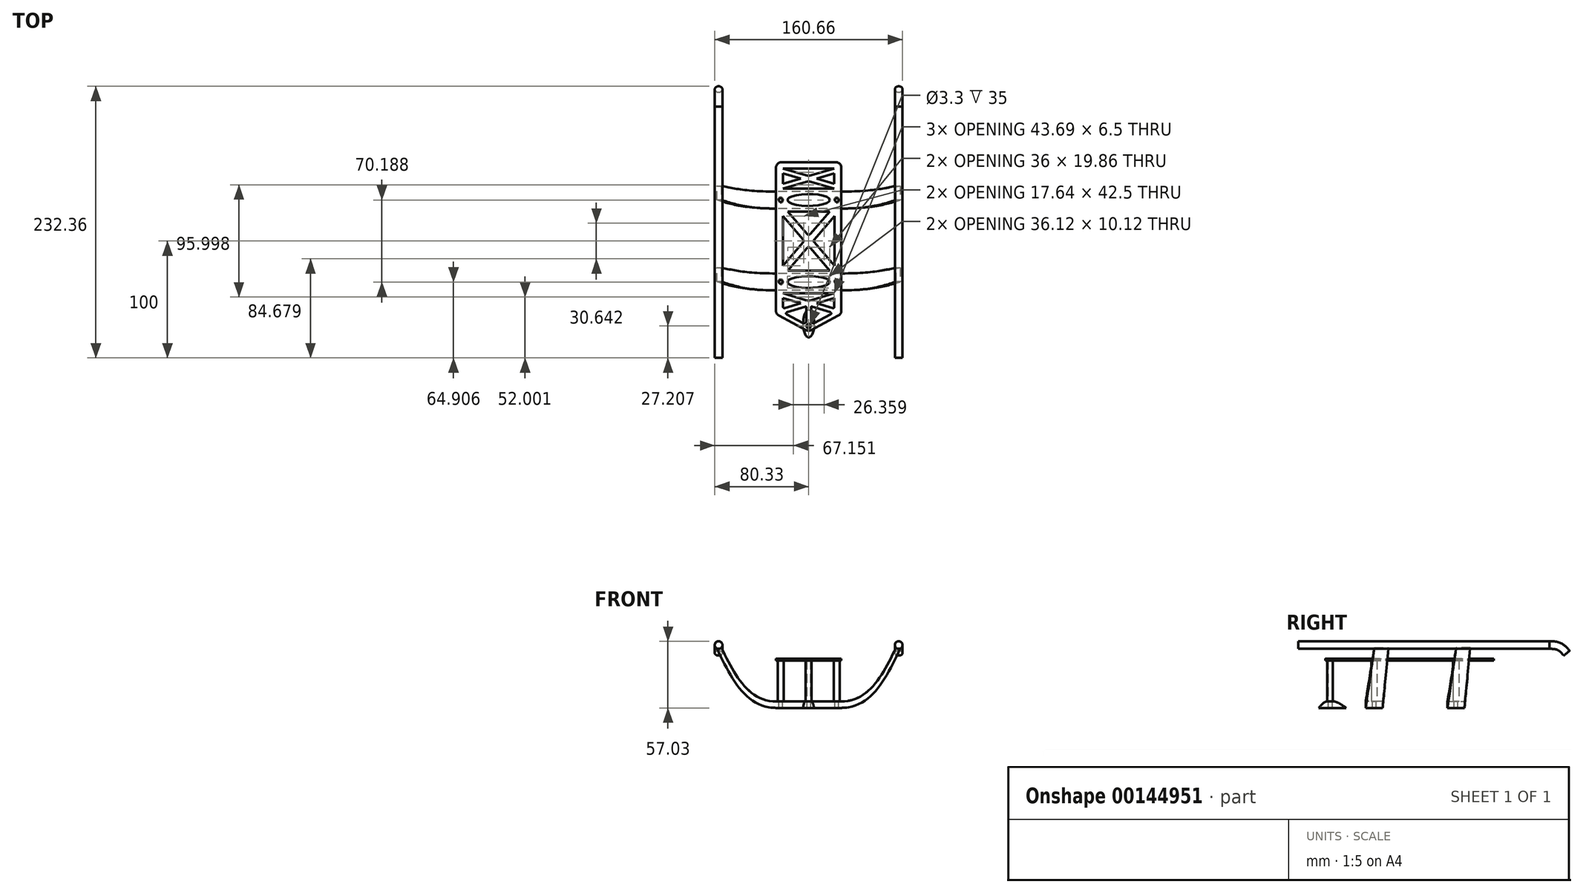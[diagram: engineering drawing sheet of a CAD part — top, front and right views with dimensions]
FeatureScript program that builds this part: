
annotation { "Feature Type Name" : "Feature", "Feature Type Description" : "" }
export const myFeature = defineFeature(function(context is Context, id is Id, definition is map)
    precondition{}
    {
        {
            var Q0;
            Q0=qCreatedBy(makeId("Top.planeOp"),FACE);
            var sketch = newSketch(context, id + "F0", { "sketchPlane" : qUnion([Q0])});
            skCircle(sketch, "E0", {"center": v(24, 35) * mm, "radius": 1.55 * mm});
            skCircle(sketch, "E1.MirrorC", {"center": v(-24, 35) * mm, "radius": 1.55 * mm});
            skCircle(sketch, "E2.MirrorC", {"center": v(-24, -35) * mm, "radius": 1.55 * mm});
            skCircle(sketch, "E3.MirrorC", {"center": v(24, -35) * mm, "radius": 1.55 * mm});
            skLineSegment(sketch, "E4.bottom", {"start": v(27.5, 27.75) * mm, "end": v(-27.5, 27.75) * mm});
            skLineSegment(sketch, "E4.top", {"start": v(27.5, 42.25) * mm, "end": v(-27.5, 42.25) * mm});
            skLineSegment(sketch, "E4.left", {"start": v(27.5, 27.75) * mm, "end": v(27.5, 42.25) * mm});
            skLineSegment(sketch, "E4.right", {"start": v(-27.5, 27.75) * mm, "end": v(-27.5, 42.25) * mm});
            skPoint(sketch, "E4.middle", {"position": v(0, 35) * mm});
            skPoint(sketch, "E5.MirrorP", {"position": v(0, -35) * mm});
            skLineSegment(sketch, "E6.MirrorCS", {"start": v(-27.5, -27.75) * mm, "end": v(-27.5, -42.25) * mm});
            skLineSegment(sketch, "E7.MirrorCS", {"start": v(27.5, -27.75) * mm, "end": v(27.5, -42.25) * mm});
            skLineSegment(sketch, "E8.MirrorCS", {"start": v(27.5, -27.75) * mm, "end": v(-27.5, -27.75) * mm});
            skLineSegment(sketch, "E9.MirrorCS", {"start": v(27.5, -42.25) * mm, "end": v(-27.5, -42.25) * mm});
            skSolve(sketch);
        }
        {
            var Q0;
            Q0=qSketchRegion(id+"F0",true);
            extrude(context, id + "F1", {"entities" : qUnion([Q0]), "oppositeDirection" : true, "depth" : 5.5 * mm});
        }
        {
            var Q0;
            Q0=makeQuery(id+"F1.opExtrude","CAP_FACE",FACE,{"disambiguationData":[OSD([sQuery(id+"F0.wireOp",EDGE,"E0"),sQuery(id+"F0.wireOp",EDGE,"E1.MirrorC"),sQuery(id+"F0.wireOp",EDGE,"E4.bottom"),sQuery(id+"F0.wireOp",EDGE,"E4.top"),sQuery(id+"F0.wireOp",EDGE,"E4.left"),sQuery(id+"F0.wireOp",EDGE,"E4.right")])],"isStart":true});
            cPlane(context, id + "F2", {"entities" : qUnion([Q0]), "cplaneType" : CPlaneType.OFFSET, "offset" : 47 * mm, "width" : 150 * mm, "height" : 150 * mm});
        }
        {
            var Q0;
            Q0=qCreatedBy(id+"F2.planeOp",FACE);
            var sketch = newSketch(context, id + "F3", { "sketchPlane" : qUnion([Q0])});
            skLineSegment(sketch, "E10.bottom", {"start": v(-79, 47.25) * mm, "end": v(-75, 47.25) * mm});
            skLineSegment(sketch, "E10.top", {"start": v(-79, 35.25) * mm, "end": v(-75, 35.25) * mm});
            skLineSegment(sketch, "E10.left", {"start": v(-79, 47.25) * mm, "end": v(-79, 35.25) * mm});
            skLineSegment(sketch, "E10.right", {"start": v(-75, 47.25) * mm, "end": v(-75, 35.25) * mm});
            skLineSegment(sketch, "E11.bottom", {"start": v(-79, -22.75) * mm, "end": v(-75, -22.75) * mm});
            skLineSegment(sketch, "E11.top", {"start": v(-79, -34.75) * mm, "end": v(-75, -34.75) * mm});
            skLineSegment(sketch, "E11.left", {"start": v(-79, -22.75) * mm, "end": v(-79, -34.75) * mm});
            skLineSegment(sketch, "E11.right", {"start": v(-75, -22.75) * mm, "end": v(-75, -34.75) * mm});
            skLineSegment(sketch, "E12.MirrorCS", {"start": v(79, 47.25) * mm, "end": v(75, 47.25) * mm});
            skLineSegment(sketch, "E13.MirrorCS", {"start": v(79, 35.25) * mm, "end": v(75, 35.25) * mm});
            skLineSegment(sketch, "E14.MirrorCS", {"start": v(79, 47.25) * mm, "end": v(79, 35.25) * mm});
            skLineSegment(sketch, "E15.MirrorCS", {"start": v(75, 47.25) * mm, "end": v(75, 35.25) * mm});
            skLineSegment(sketch, "E16.MirrorCS", {"start": v(79, -22.75) * mm, "end": v(75, -22.75) * mm});
            skLineSegment(sketch, "E17.MirrorCS", {"start": v(79, -34.75) * mm, "end": v(75, -34.75) * mm});
            skLineSegment(sketch, "E18.MirrorCS", {"start": v(75, -22.75) * mm, "end": v(75, -34.75) * mm});
            skLineSegment(sketch, "E19.MirrorCS", {"start": v(79, -22.75) * mm, "end": v(79, -34.75) * mm});
            skSolve(sketch);
        }
        {
            var Q0;
            Q0=qSketchRegion(id+"F3",true);
            extrude(context, id + "F4", {"entities" : qUnion([Q0]), "depth" : 1 * mm, "symmetric" : true});
        }
        {
            var Q0;
            Q0=makeQuery(id+"F1.opExtrude","SWEPT_FACE",FACE,{"disambiguationData":[OSD([sQuery(id+"F0.wireOp",EDGE,"E4.right")])]});
            var Q1;
            Q1=makeQuery(id+"F4.opExtrude","CAP_FACE",FACE,{"disambiguationData":[OSD([sQuery(id+"F3.wireOp",EDGE,"E10.bottom"),sQuery(id+"F3.wireOp",EDGE,"E10.top"),sQuery(id+"F3.wireOp",EDGE,"E10.left"),sQuery(id+"F3.wireOp",EDGE,"E10.right")])],"isStart":true});
            loft(context, id + "F5", {"operationType" : NewBodyOperationType.ADD, "startCondition" : LoftEndDerivativeType.NORMAL_TO_PROFILE, "startMagnitude" : 1.5, "sheetProfilesArray" : [{ "sheetProfileEntities" : qUnion([Q0]) }, { "sheetProfileEntities" : qUnion([Q1]) }]});
        }
        {
            var Q0;
            Q0=makeQuery(id+"F1.opExtrude","SWEPT_FACE",FACE,{"disambiguationData":[OSD([sQuery(id+"F0.wireOp",EDGE,"E6.MirrorCS")])]});
            var Q1;
            Q1=makeQuery(id+"F4.opExtrude","CAP_FACE",FACE,{"disambiguationData":[OSD([sQuery(id+"F3.wireOp",EDGE,"E11.bottom"),sQuery(id+"F3.wireOp",EDGE,"E11.top"),sQuery(id+"F3.wireOp",EDGE,"E11.left"),sQuery(id+"F3.wireOp",EDGE,"E11.right")])],"isStart":true});
            loft(context, id + "F6", {"operationType" : NewBodyOperationType.ADD, "startCondition" : LoftEndDerivativeType.NORMAL_TO_PROFILE, "startMagnitude" : 1.5, "sheetProfilesArray" : [{ "sheetProfileEntities" : qUnion([Q0]) }, { "sheetProfileEntities" : qUnion([Q1]) }]});
        }
        {
            var Q0;
            Q0=makeQuery(id+"F1.opExtrude","SWEPT_FACE",FACE,{"disambiguationData":[OSD([sQuery(id+"F0.wireOp",EDGE,"E7.MirrorCS")])]});
            var Q1;
            Q1=makeQuery(id+"F4.opExtrude","CAP_FACE",FACE,{"disambiguationData":[OSD([sQuery(id+"F3.wireOp",EDGE,"E16.MirrorCS"),sQuery(id+"F3.wireOp",EDGE,"E17.MirrorCS"),sQuery(id+"F3.wireOp",EDGE,"E18.MirrorCS"),sQuery(id+"F3.wireOp",EDGE,"E19.MirrorCS")])],"isStart":true});
            loft(context, id + "F7", {"operationType" : NewBodyOperationType.ADD, "startCondition" : LoftEndDerivativeType.NORMAL_TO_PROFILE, "startMagnitude" : 1.5, "sheetProfilesArray" : [{ "sheetProfileEntities" : qUnion([Q0]) }, { "sheetProfileEntities" : qUnion([Q1]) }]});
        }
        {
            var Q0;
            Q0=makeQuery(id+"F1.opExtrude","SWEPT_FACE",FACE,{"disambiguationData":[OSD([sQuery(id+"F0.wireOp",EDGE,"E4.left")])]});
            var Q1;
            Q1=makeQuery(id+"F4.opExtrude","CAP_FACE",FACE,{"disambiguationData":[OSD([sQuery(id+"F3.wireOp",EDGE,"E12.MirrorCS"),sQuery(id+"F3.wireOp",EDGE,"E13.MirrorCS"),sQuery(id+"F3.wireOp",EDGE,"E14.MirrorCS"),sQuery(id+"F3.wireOp",EDGE,"E15.MirrorCS")])],"isStart":true});
            loft(context, id + "F8", {"operationType" : NewBodyOperationType.ADD, "startCondition" : LoftEndDerivativeType.NORMAL_TO_PROFILE, "startMagnitude" : 1.5, "sheetProfilesArray" : [{ "sheetProfileEntities" : qUnion([Q0]) }, { "sheetProfileEntities" : qUnion([Q1]) }]});
        }
        {
            var Q0;
            Q0=qCreatedBy(makeId("Front.planeOp"),FACE);
            var sketch = newSketch(context, id + "F9", { "sketchPlane" : qUnion([Q0])});
            skCircle(sketch, "E20", {"center": v(-77.08, 48.25) * mm, "radius": 3.25 * mm});
            skCircle(sketch, "E21.MirrorC", {"center": v(77.08, 48.25) * mm, "radius": 3.25 * mm});
            skSolve(sketch);
        }
        {
            var Q0;
            Q0=qSketchRegion(id+"F9",true);
            extrude(context, id + "F10", {"entities" : qUnion([Q0]), "operationType" : NewBodyOperationType.ADD, "depth" : 100 * mm, "hasSecondDirection" : true, "secondDirectionOppositeDirection" : true, "secondDirectionDepth" : 115 * mm});
        }
        {
            var Q0;
            Q0=qCreatedBy(makeId("Right.planeOp"),FACE);
            var sketch = newSketch(context, id + "F11", { "sketchPlane" : qUnion([Q0])});
            skFitSpline(sketch, "E22", {"points": [v(115, 54.9) * mm, v(123.56, 53.94) * mm, v(128.8, 51.44) * mm, v(135, 45.49) * mm], "startDerivative": vector(20.16, 0.9) * mm, "endDerivative": vector(29.36, -33.3) * mm});
            skPoint(sketch, "E23", {"position": v(115, 57.99) * mm});
            skSolve(sketch);
        }
        {
            var Q0;
            Q0=makeQuery(id+"F10.opExtrude","CAP_FACE",FACE,{"disambiguationData":[OSD([sQuery(id+"F9.wireOp",EDGE,"E20")])],"isStart":true});
            var Q1;
            Q1=makeQuery(id+"F10.opExtrude","CAP_FACE",FACE,{"disambiguationData":[OSD([sQuery(id+"F9.wireOp",EDGE,"E21.MirrorC")])],"isStart":true});
            var Q2;
            Q2=sQuery(id+"F11.wireOp",EDGE,"E22");
            sweep(context, id + "F12", {"operationType" : NewBodyOperationType.ADD, "profiles" : qUnion([Q0, Q1]), "path" : qUnion([Q2])});
        }
        {
            var Q0;
            Q0=makeQuery(id+"F1.opExtrude","CAP_FACE",FACE,{"disambiguationData":[OSD([sQuery(id+"F0.wireOp",EDGE,"E0"),sQuery(id+"F0.wireOp",EDGE,"E1.MirrorC"),sQuery(id+"F0.wireOp",EDGE,"E4.bottom"),sQuery(id+"F0.wireOp",EDGE,"E4.top"),sQuery(id+"F0.wireOp",EDGE,"E4.left"),sQuery(id+"F0.wireOp",EDGE,"E4.right")])],"isStart":true});
            cPlane(context, id + "F13", {"entities" : qUnion([Q0]), "cplaneType" : CPlaneType.OFFSET, "offset" : 35 * mm, "width" : 150 * mm, "height" : 150 * mm});
        }
        {
            var Q0;
            Q0=qCreatedBy(id+"F13.planeOp",FACE);
            var sketch = newSketch(context, id + "F14", { "sketchPlane" : qUnion([Q0])});
            skLineSegment(sketch, "E24.top", {"start": v(23, 67.5) * mm, "end": v(-23, 67.5) * mm});
            skLineSegment(sketch, "E24.left", {"start": v(28, -59.49) * mm, "end": v(28, 62.5) * mm});
            skLineSegment(sketch, "E24.right", {"start": v(-28, -59.49) * mm, "end": v(-28, 62.5) * mm});
            skLineSegment(sketch, "E25", {"start": v(21.85, -56.49) * mm, "end": v(21.85, -48.92) * mm});
            skLineSegment(sketch, "E26", {"start": v(21.85, -48.92) * mm, "end": v(6.88, -53.37) * mm});
            skLineSegment(sketch, "E27", {"start": v(6.88, -53.37) * mm, "end": v(20.56, -57.44) * mm});
            skLineSegment(sketch, "E28.MirrorCS", {"start": v(-6.88, -53.37) * mm, "end": v(-20.56, -57.44) * mm});
            skLineSegment(sketch, "E29.MirrorCS", {"start": v(-21.85, -56.49) * mm, "end": v(-21.85, -48.92) * mm});
            skLineSegment(sketch, "E30.MirrorCS", {"start": v(-21.85, -48.92) * mm, "end": v(-6.88, -53.37) * mm});
            skLineSegment(sketch, "E31", {"start": v(2.64, -56.29) * mm, "end": v(18.57, -61.03) * mm});
            skLineSegment(sketch, "E32", {"start": v(2.98, -53.37) * mm, "end": v(-2.47, -53.37) * mm});
            skLineSegment(sketch, "E33.MirrorCS", {"start": v(0, -51.25) * mm, "end": v(21.85, -44.75) * mm});
            skLineSegment(sketch, "E34.MirrorCS", {"start": v(21.85, -44.75) * mm, "end": v(-21.85, -44.75) * mm});
            skLineSegment(sketch, "E35.MirrorCS", {"start": v(-21.85, -44.75) * mm, "end": v(0, -51.25) * mm});
            skLineSegment(sketch, "E36.MirrorCS", {"start": v(2.98, 53.37) * mm, "end": v(-2.47, 53.37) * mm});
            skLineSegment(sketch, "E37.MirrorCS", {"start": v(-21.85, 62) * mm, "end": v(0, 55.5) * mm});
            skLineSegment(sketch, "E38.MirrorCS", {"start": v(0, 55.5) * mm, "end": v(21.85, 62) * mm});
            skLineSegment(sketch, "E39.MirrorCS", {"start": v(6.88, 53.37) * mm, "end": v(21.85, 57.83) * mm});
            skLineSegment(sketch, "E40.MirrorCS", {"start": v(21.85, 57.83) * mm, "end": v(21.85, 48.92) * mm});
            skLineSegment(sketch, "E41.MirrorCS", {"start": v(21.85, 48.92) * mm, "end": v(6.88, 53.37) * mm});
            skLineSegment(sketch, "E42.MirrorCS", {"start": v(-21.85, 44.75) * mm, "end": v(0, 51.25) * mm});
            skLineSegment(sketch, "E43.MirrorCS", {"start": v(21.85, 62) * mm, "end": v(-21.85, 62) * mm});
            skLineSegment(sketch, "E44.MirrorCS", {"start": v(-21.85, 48.92) * mm, "end": v(-6.88, 53.37) * mm});
            skLineSegment(sketch, "E45.MirrorCS", {"start": v(-21.85, 57.83) * mm, "end": v(-21.85, 48.92) * mm});
            skLineSegment(sketch, "E46.MirrorCS", {"start": v(-6.88, 53.37) * mm, "end": v(-21.85, 57.83) * mm});
            skLineSegment(sketch, "E47.MirrorCS", {"start": v(21.85, 44.75) * mm, "end": v(-21.85, 44.75) * mm});
            skLineSegment(sketch, "E48.MirrorCS", {"start": v(0, 51.25) * mm, "end": v(21.85, 44.75) * mm});
            skEllipse(sketch, "E49", {"center": v(0, 35.1) * mm, "majorRadius": 18.06 * mm, "minorRadius": 5.06 * mm, "majorAxis": v(1, 0)});
            skEllipse(sketch, "E50.MirrorC", {"center": v(0, -35.1) * mm, "majorRadius": 18.06 * mm, "minorRadius": 5.06 * mm, "majorAxis": v(1, 0)});
            skPoint(sketch, "E51.visualSharp", {"position": v(-28, 67.5) * mm});
            skArc(sketch, "E51.filletArc", {"start": v(-23, 67.5) * mm, "mid": v(-26.54, 66.04) * mm, "end": v(-28, 62.5) * mm});
            skPoint(sketch, "E52.visualSharp", {"position": v(28, 67.5) * mm});
            skArc(sketch, "E52.filletArc", {"start": v(28, 62.5) * mm, "mid": v(26.54, 66.04) * mm, "end": v(23, 67.5) * mm});
            skLineSegment(sketch, "E53.bottom", {"start": v(-18, 25.25) * mm, "end": v(18, 25.25) * mm});
            skLineSegment(sketch, "E53.top", {"start": v(-18, -25.25) * mm, "end": v(18, -25.25) * mm});
            skLineSegment(sketch, "E53.left", {"start": v(-22, 21.25) * mm, "end": v(-22, -21.25) * mm});
            skLineSegment(sketch, "E53.right", {"start": v(22, 21.25) * mm, "end": v(22, -21.25) * mm});
            skLineSegment(sketch, "E54", {"start": v(-18, 25.25) * mm, "end": v(-1.52, 6.09) * mm});
            skLineSegment(sketch, "E55", {"start": v(-22, 21.25) * mm, "end": v(-4.84, 1.3) * mm});
            skLineSegment(sketch, "E56", {"start": v(-22, -21.25) * mm, "end": v(-4.84, -1.3) * mm});
            skLineSegment(sketch, "E57", {"start": v(-18, -25.25) * mm, "end": v(-1.52, -6.09) * mm});
            skPoint(sketch, "E58.orphan", {"position": v(-22, 25.25) * mm});
            skPoint(sketch, "E59.orphan", {"position": v(22, 25.25) * mm});
            skPoint(sketch, "E60.orphan", {"position": v(22, -25.25) * mm});
            skPoint(sketch, "E61.orphan", {"position": v(-22, -25.25) * mm});
            skLineSegment(sketch, "E62.trimOffspring", {"start": v(1.52, -6.09) * mm, "end": v(18, -25.25) * mm});
            skLineSegment(sketch, "E63.trimOffspring", {"start": v(1.52, 6.09) * mm, "end": v(18, 25.25) * mm});
            skLineSegment(sketch, "E64.trimOffspring", {"start": v(4.84, -1.3) * mm, "end": v(22, -21.25) * mm});
            skLineSegment(sketch, "E65.trimOffspring", {"start": v(4.84, 1.3) * mm, "end": v(22, 21.25) * mm});
            skPoint(sketch, "E66.visualSharp", {"position": v(0, 4.33) * mm});
            skArc(sketch, "E66.filletArc", {"start": v(-1.52, 6.09) * mm, "mid": v(0, 5.4) * mm, "end": v(1.52, 6.09) * mm});
            skPoint(sketch, "E67.visualSharp", {"position": v(3.72, 0) * mm});
            skArc(sketch, "E67.filletArc", {"start": v(4.84, 1.3) * mm, "mid": v(4.36, 0) * mm, "end": v(4.84, -1.3) * mm});
            skPoint(sketch, "E68.visualSharp", {"position": v(0, -4.33) * mm});
            skArc(sketch, "E68.filletArc", {"start": v(1.52, -6.09) * mm, "mid": v(0, -5.4) * mm, "end": v(-1.52, -6.09) * mm});
            skPoint(sketch, "E69.visualSharp", {"position": v(-3.72, 0) * mm});
            skArc(sketch, "E69.filletArc", {"start": v(-4.84, -1.3) * mm, "mid": v(-4.36, 0) * mm, "end": v(-4.84, 1.3) * mm});
            skArc(sketch, "E70", {"start": v(-1.87, -76.33) * mm, "mid": v(0, -76.8) * mm, "end": v(1.87, -76.33) * mm});
            skLineSegment(sketch, "E71", {"start": v(1.87, -76.33) * mm, "end": v(25.34, -63.9) * mm});
            skLineSegment(sketch, "E72.MirrorCS", {"start": v(-1.87, -76.33) * mm, "end": v(-25.34, -63.9) * mm});
            skPoint(sketch, "E73.visualSharp", {"position": v(-28, -62.5) * mm});
            skArc(sketch, "E73.filletArc", {"start": v(-28, -59.49) * mm, "mid": v(-27.28, -62.07) * mm, "end": v(-25.34, -63.9) * mm});
            skPoint(sketch, "E74.visualSharp", {"position": v(28, -62.5) * mm});
            skArc(sketch, "E74.filletArc", {"start": v(25.34, -63.9) * mm, "mid": v(27.28, -62.07) * mm, "end": v(28, -59.49) * mm});
            skLineSegment(sketch, "E75.MirrorCS", {"start": v(-2.64, -56.29) * mm, "end": v(-18.57, -61.03) * mm});
            skLineSegment(sketch, "E76", {"start": v(-18.75, -62.87) * mm, "end": v(-5.03, -70.13) * mm});
            skArc(sketch, "E77", {"start": v(-5.03, -70.13) * mm, "mid": v(-3.81, -70.35) * mm, "end": v(-2.7, -69.84) * mm});
            skLineSegment(sketch, "E78.MirrorCS", {"start": v(18.75, -62.87) * mm, "end": v(5.03, -70.13) * mm});
            skArc(sketch, "E79.MirrorCS", {"start": v(5.03, -70.13) * mm, "mid": v(3.81, -70.35) * mm, "end": v(2.7, -69.84) * mm});
            skArc(sketch, "E80.trimOffspring", {"start": v(2.7, -69.84) * mm, "mid": v(2.55, -69.71) * mm, "end": v(2.4, -69.6) * mm});
            skCircle(sketch, "E81", {"center": v(0, -72.8) * mm, "radius": 1.55 * mm});
            skPoint(sketch, "E82.visualSharp", {"position": v(-20.92, -61.72) * mm});
            skArc(sketch, "E82.filletArc", {"start": v(-18.57, -61.03) * mm, "mid": v(-19.28, -61.89) * mm, "end": v(-18.75, -62.87) * mm});
            skPoint(sketch, "E83.visualSharp", {"position": v(20.92, -61.72) * mm});
            skArc(sketch, "E83.filletArc", {"start": v(18.75, -62.87) * mm, "mid": v(19.28, -61.89) * mm, "end": v(18.57, -61.03) * mm});
            skPoint(sketch, "E84.visualSharp", {"position": v(21.85, -57.83) * mm});
            skArc(sketch, "E84.filletArc", {"start": v(20.56, -57.44) * mm, "mid": v(21.44, -57.29) * mm, "end": v(21.85, -56.49) * mm});
            skPoint(sketch, "E85.visualSharp", {"position": v(-21.85, -57.83) * mm});
            skArc(sketch, "E85.filletArc", {"start": v(-21.85, -56.49) * mm, "mid": v(-21.44, -57.29) * mm, "end": v(-20.56, -57.44) * mm});
            skLineSegment(sketch, "E86", {"start": v(-2, -56.76) * mm, "end": v(-2, -68.8) * mm});
            skLineSegment(sketch, "E87.MirrorCS", {"start": v(2, -56.76) * mm, "end": v(2, -68.8) * mm});
            skPoint(sketch, "E88.newPointA", {"position": v(-2, -56.1) * mm});
            skPoint(sketch, "E88.newPointB", {"position": v(0, -55.5) * mm});
            skArc(sketch, "E88.filletArc", {"start": v(-2, -56.76) * mm, "mid": v(-2.2, -56.36) * mm, "end": v(-2.64, -56.29) * mm});
            skPoint(sketch, "E89.newPointA", {"position": v(2, -56.1) * mm});
            skArc(sketch, "E89.filletArc", {"start": v(2.64, -56.29) * mm, "mid": v(2.2, -56.36) * mm, "end": v(2, -56.76) * mm});
            skArc(sketch, "E90.trimOffspring", {"start": v(-2.4, -69.6) * mm, "mid": v(-2.55, -69.71) * mm, "end": v(-2.7, -69.84) * mm});
            skPoint(sketch, "E91.visualSharp", {"position": v(2, -69.33) * mm});
            skArc(sketch, "E91.filletArc", {"start": v(2, -68.8) * mm, "mid": v(2.1, -69.24) * mm, "end": v(2.4, -69.6) * mm});
            skPoint(sketch, "E92.visualSharp", {"position": v(-2, -69.33) * mm});
            skArc(sketch, "E92.filletArc", {"start": v(-2.4, -69.6) * mm, "mid": v(-2.1, -69.24) * mm, "end": v(-2, -68.8) * mm});
            skSolve(sketch);
        }
        {
            var Q0;
            Q0=qSketchRegion(id+"F14",true);
            extrude(context, id + "F15", {"entities" : qUnion([Q0]), "depth" : 1.5 * mm});
        }
        {
            var Q0;
            Q0=makeQuery(id+"F0.imprint","IMPRINT",FACE,{"disambiguationData":[TD([[makeQuery(id+"F0.imprint","IMPRINT",EDGE,{"derivedFrom":sQuery(id+"F0.wireOp",EDGE,"E3.MirrorC")}),1.0]])]});
            var sketch = newSketch(context, id + "F16", { "sketchPlane" : qUnion([Q0])});
            skEllipse(sketch, "E93", {"center": v(0, -72.8) * mm, "majorRadius": 2.5 * mm, "minorRadius": 2.5 * mm, "majorAxis": v(0, 1)});
            skLineSegment(sketch, "E94", {"start": v(0, -72.8) * mm, "end": v(0, -75.3) * mm});
            skSolve(sketch);
        }
        {
            var Q0;
            Q0=makeQuery(id+"F1.opExtrude","CAP_FACE",FACE,{"disambiguationData":[OSD([sQuery(id+"F0.wireOp",EDGE,"E3.MirrorC"),sQuery(id+"F0.wireOp",EDGE,"E2.MirrorC"),sQuery(id+"F0.wireOp",EDGE,"E6.MirrorCS"),sQuery(id+"F0.wireOp",EDGE,"E7.MirrorCS"),sQuery(id+"F0.wireOp",EDGE,"E8.MirrorCS"),sQuery(id+"F0.wireOp",EDGE,"E9.MirrorCS")])],"isStart":false});
            var sketch = newSketch(context, id + "F17", { "sketchPlane" : qUnion([Q0])});
            skEllipse(sketch, "E95", {"center": v(0, 70.72) * mm, "majorRadius": 11.75 * mm, "minorRadius": 4.76 * mm, "majorAxis": v(0, -1)});
            skLineSegment(sketch, "E96", {"start": v(0, 70.72) * mm, "end": v(0, 82.47) * mm});
            skSolve(sketch);
        }
        {
            var Q1;
            Q1=qSketchRegion(id+"F16",true);
            var Q2;
            Q2=qSketchRegion(id+"F17",true);
            loft(context, id + "F18", {"startCondition" : LoftEndDerivativeType.TANGENT_TO_PROFILE, "startMagnitude" : 1, "sheetProfilesArray" : [{ "sheetProfileEntities" : qUnion([Q1]) }, { "sheetProfileEntities" : qUnion([Q2]) }]});
        }
        {
            var Q0;
            Q0=makeQuery(id+"F15.opExtrude","CAP_FACE",FACE,{"disambiguationData":[OSD([sQuery(id+"F14.wireOp",EDGE,"E24.bottom"),sQuery(id+"F14.wireOp",EDGE,"E24.top"),sQuery(id+"F14.wireOp",EDGE,"E24.left"),sQuery(id+"F14.wireOp",EDGE,"E24.right"),sQuery(id+"F14.wireOp",EDGE,"E25"),sQuery(id+"F14.wireOp",EDGE,"E26"),sQuery(id+"F14.wireOp",EDGE,"E27"),sQuery(id+"F14.wireOp",EDGE,"E28.MirrorCS"),sQuery(id+"F14.wireOp",EDGE,"E29.MirrorCS"),sQuery(id+"F14.wireOp",EDGE,"E30.MirrorCS"),sQuery(id+"F14.wireOp",EDGE,"kgWpuRN8-z3XB-NoYH-Fo3q-VtEeIHUye6mg"),sQuery(id+"F14.wireOp",EDGE,"PAQE7tgt-a42U-32r6-Kom9-lAOUVqeRcCwj"),sQuery(id+"F14.wireOp",EDGE,"E31"),sQuery(id+"F14.wireOp",EDGE,"E33.MirrorCS"),sQuery(id+"F14.wireOp",EDGE,"E34.MirrorCS"),sQuery(id+"F14.wireOp",EDGE,"E35.MirrorCS"),sQuery(id+"F14.wireOp",EDGE,"E37.MirrorCS"),sQuery(id+"F14.wireOp",EDGE,"E38.MirrorCS"),sQuery(id+"F14.wireOp",EDGE,"E39.MirrorCS"),sQuery(id+"F14.wireOp",EDGE,"E40.MirrorCS"),sQuery(id+"F14.wireOp",EDGE,"E41.MirrorCS"),sQuery(id+"F14.wireOp",EDGE,"E42.MirrorCS"),sQuery(id+"F14.wireOp",EDGE,"E43.MirrorCS"),sQuery(id+"F14.wireOp",EDGE,"E44.MirrorCS"),sQuery(id+"F14.wireOp",EDGE,"E45.MirrorCS"),sQuery(id+"F14.wireOp",EDGE,"E46.MirrorCS"),sQuery(id+"F14.wireOp",EDGE,"E47.MirrorCS"),sQuery(id+"F14.wireOp",EDGE,"E48.MirrorCS"),sQuery(id+"F14.wireOp",EDGE,"41cgnIPL-npWc-O3OT-IIvp-3opdmebJhPuE"),sQuery(id+"F14.wireOp",EDGE,"cnqzEcAR-puum-2v5H-bPeM-nhvkTepjbg7f"),sQuery(id+"F14.wireOp",EDGE,"ZUyBv95D-Vip0-E0xQ-HOKZ-qXVskTSMhhZ4"),sQuery(id+"F14.wireOp",EDGE,"QW4Knzpe-XfPx-6G3O-fQ7r-xCA8DHTI8llc"),sQuery(id+"F14.wireOp",EDGE,"u5ZCEIEt-8dGf-CeKo-rW56-BvbBlPJxl9Av"),sQuery(id+"F14.wireOp",EDGE,"tRerhao7-xNC6-3Qj8-PqBg-vBzmJME0fykC"),sQuery(id+"F14.wireOp",EDGE,"34f72953-b367-436d-b2e1-794d6ac8d1dc0.MirrorCS"),sQuery(id+"F14.wireOp",EDGE,"e1a0620d-9711-44c7-a052-cdfd6f5fabb40.MirrorCS"),sQuery(id+"F14.wireOp",EDGE,"f9968c47-6fa3-4d05-afce-87440d7f02980.MirrorCS"),sQuery(id+"F14.wireOp",EDGE,"cde4a5db-1fe4-4333-8411-bf7d7e01e0120.MirrorCS"),sQuery(id+"F14.wireOp",EDGE,"0ad4e2a6-e274-4dd3-8f10-cc4f6a0458050.MirrorCS"),sQuery(id+"F14.wireOp",EDGE,"46e521f6-c0f6-47cd-9bc7-52dcf3b3e5ab0.MirrorCS"),sQuery(id+"F14.wireOp",EDGE,"E49"),sQuery(id+"F14.wireOp",EDGE,"E50.MirrorC"),sQuery(id+"F14.wireOp",EDGE,"E51.filletArc"),sQuery(id+"F14.wireOp",EDGE,"E52.filletArc"),sQuery(id+"F14.wireOp",EDGE,"2506973a-7fd9-4c85-8d00-4ddd12030c14.filletArc"),sQuery(id+"F14.wireOp",EDGE,"d070286b-625e-487d-9c83-938932120a88.filletArc")])],"isStart":true});
            var sketch = newSketch(context, id + "F19", { "sketchPlane" : qUnion([Q0])});
            skCircle(sketch, "E97", {"center": v(0, 72.8) * mm, "radius": 2.5 * mm});
            skSolve(sketch);
        }
        {
            var Q0;
            Q0=qSketchRegion(id+"F19",true);
            var Q1;
            Q1=makeQuery(id+"F18.opLoft","CAP_FACE",FACE,{"disambiguationData":[OSD([makeQuery(id+"F16.imprint","IMPRINT",FACE,{"disambiguationData":[TD([[makeQuery(id+"F16.imprint","IMPRINT",EDGE,{"derivedFrom":sQuery(id+"F16.wireOp",EDGE,"E93")}),1.0]])]})])],"isStart":true});
            extrude(context, id + "F20", {"entities" : qUnion([Q0]), "endBound" : BoundingType.UP_TO_SURFACE, "endBoundEntityFace" : qUnion([Q1]), "depth" : 25 * mm});
        }
        {
            var Q0;
            Q0=makeQuery(id+"F18.opLoft","CAP_FACE",FACE,{"disambiguationData":[OSD([makeQuery(id+"F17.imprint","IMPRINT",FACE,{"disambiguationData":[TD([[makeQuery(id+"F17.imprint","IMPRINT",EDGE,{"derivedFrom":sQuery(id+"F17.wireOp",EDGE,"E95")}),1.0]])]})])],"isStart":true});
            var sketch = newSketch(context, id + "F21", { "sketchPlane" : qUnion([Q0])});
            skCircle(sketch, "E98", {"center": v(0, 72.8) * mm, "radius": 1.65 * mm});
            skSolve(sketch);
        }
        {
            var Q0;
            Q0=qSketchRegion(id+"F21",true);
            extrude(context, id + "F22", {"entities" : qUnion([Q0]), "operationType" : NewBodyOperationType.REMOVE, "endBound" : BoundingType.THROUGH_ALL, "oppositeDirection" : true, "depth" : 25 * mm});
        }
        {
            var Q0;
            Q0=makeQuery(id+"F15.opExtrude","CAP_FACE",FACE,{"disambiguationData":[OSD([sQuery(id+"F14.wireOp",EDGE,"E24.bottom"),sQuery(id+"F14.wireOp",EDGE,"E24.top"),sQuery(id+"F14.wireOp",EDGE,"E24.left"),sQuery(id+"F14.wireOp",EDGE,"E24.right")])],"isStart":false});
            var sketch = newSketch(context, id + "F23", { "sketchPlane" : qUnion([Q0])});
            skCircle(sketch, "E99", {"center": v(-24, 35) * mm, "radius": 1.55 * mm});
            skCircle(sketch, "E100", {"center": v(24, 35) * mm, "radius": 1.55 * mm});
            skCircle(sketch, "E101", {"center": v(-24, -35) * mm, "radius": 1.55 * mm});
            skCircle(sketch, "E102", {"center": v(24, -35) * mm, "radius": 1.55 * mm});
            skSolve(sketch);
        }
        {
            var Q0;
            Q0=qSketchRegion(id+"F23",true);
            var Q1;
            Q1=makeQuery(id+"F15.opExtrude","CAP_FACE",FACE,{"disambiguationData":[OSD([sQuery(id+"F14.wireOp",EDGE,"E24.bottom"),sQuery(id+"F14.wireOp",EDGE,"E24.top"),sQuery(id+"F14.wireOp",EDGE,"E24.left"),sQuery(id+"F14.wireOp",EDGE,"E24.right")])],"isStart":true});
            extrude(context, id + "F24", {"entities" : qUnion([Q0]), "operationType" : NewBodyOperationType.REMOVE, "endBound" : BoundingType.UP_TO_SURFACE, "oppositeDirection" : true, "endBoundEntityFace" : qUnion([Q1]), "depth" : 25 * mm});
        }
        {
            var Q0;
            Q0=makeQuery(id+"F0.imprint","IMPRINT",FACE,{"disambiguationData":[TD([[makeQuery(id+"F0.imprint","IMPRINT",EDGE,{"derivedFrom":sQuery(id+"F0.wireOp",EDGE,"E0")}),-1.0]])]});
            var sketch = newSketch(context, id + "F25", { "sketchPlane" : qUnion([Q0])});
            skCircle(sketch, "E103", {"center": v(-24, 35) * mm, "radius": 2.5 * mm});
            skCircle(sketch, "E104", {"center": v(24, 35) * mm, "radius": 2.5 * mm});
            skCircle(sketch, "E105", {"center": v(-24, -35) * mm, "radius": 2.5 * mm});
            skCircle(sketch, "E106", {"center": v(24, -35) * mm, "radius": 2.5 * mm});
            skSolve(sketch);
        }
        {
            var Q0;
            Q0=qSketchRegion(id+"F25",true);
            var Q1;
            Q1=makeQuery(id+"F15.opExtrude","CAP_FACE",FACE,{"disambiguationData":[OSD([sQuery(id+"F14.wireOp",EDGE,"E24.bottom"),sQuery(id+"F14.wireOp",EDGE,"E24.top"),sQuery(id+"F14.wireOp",EDGE,"E24.left"),sQuery(id+"F14.wireOp",EDGE,"E24.right")])],"isStart":true});
            extrude(context, id + "F26", {"entities" : qUnion([Q0]), "endBound" : BoundingType.UP_TO_SURFACE, "endBoundEntityFace" : qUnion([Q1]), "depth" : 25 * mm});
        }
    });
